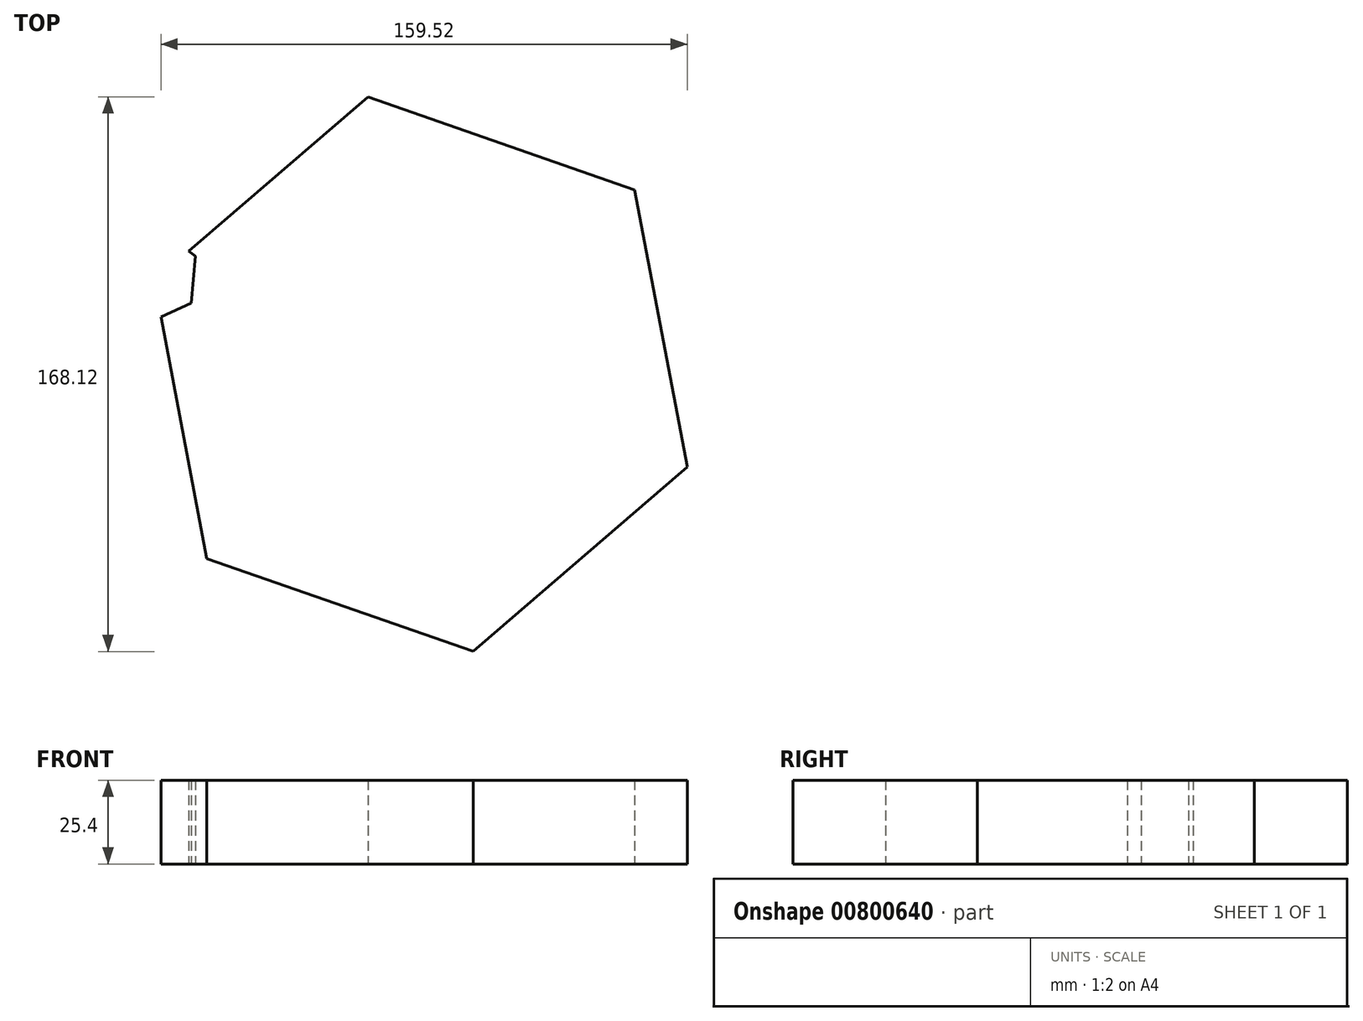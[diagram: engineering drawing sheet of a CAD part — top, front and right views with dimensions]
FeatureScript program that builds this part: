
annotation { "Feature Type Name" : "Feature", "Feature Type Description" : "" }
export const myFeature = defineFeature(function(context is Context, id is Id, definition is map)
    precondition{}
    {
        {
            var Q0;
            Q0=qCreatedBy(makeId("Top.planeOp"),FACE);
            var sketch = newSketch(context, id + "F0", { "sketchPlane" : qUnion([Q0])});
            skCircle(sketch, "E0.cCircle", {"center": v(0, 0) * mm, "radius": 74.1 * mm, "construction": true});
            skLineSegment(sketch, "E0.0", {"start": v(-16, 84.06) * mm, "end": v(64.8, 55.88) * mm});
            skLineSegment(sketch, "E0.1", {"start": v(64.8, 55.88) * mm, "end": v(80.8, -28.17) * mm});
            skLineSegment(sketch, "E0.2", {"start": v(80.8, -28.17) * mm, "end": v(16, -84.06) * mm});
            skLineSegment(sketch, "E0.3", {"start": v(16, -84.06) * mm, "end": v(-64.8, -55.88) * mm});
            skLineSegment(sketch, "E0.4", {"start": v(-64.8, -55.88) * mm, "end": v(-80.8, 28.17) * mm});
            skLineSegment(sketch, "E0.5", {"start": v(-80.8, 28.17) * mm, "end": v(-16, 84.06) * mm});
            skPoint(sketch, "E0.0.midPoint", {"position": v(24.4, 69.97) * mm});
            skCircle(sketch, "E1.cCircle", {"center": v(-81.17, 29.82) * mm, "radius": 12.37 * mm, "construction": true});
            skLineSegment(sketch, "E1.0", {"start": v(-68.2, 35.82) * mm, "end": v(-69.5, 21.59) * mm});
            skLineSegment(sketch, "E1.1", {"start": v(-69.5, 21.59) * mm, "end": v(-82.46, 15.59) * mm});
            skLineSegment(sketch, "E1.2", {"start": v(-82.46, 15.59) * mm, "end": v(-94.14, 23.82) * mm});
            skLineSegment(sketch, "E1.3", {"start": v(-94.14, 23.82) * mm, "end": v(-92.85, 38.05) * mm});
            skLineSegment(sketch, "E1.4", {"start": v(-92.85, 38.05) * mm, "end": v(-79.88, 44.05) * mm});
            skLineSegment(sketch, "E1.5", {"start": v(-79.88, 44.05) * mm, "end": v(-68.2, 35.82) * mm});
            skPoint(sketch, "E1.0.midPoint", {"position": v(-68.85, 28.7) * mm});
            skSolve(sketch);
        }
        {
            var Q0;
            {var subQ1=sQuery(id+"F0.wireOp",EDGE,"E0.0");Q0=makeQuery(id+"F0.imprint","IMPRINT",FACE,{"disambiguationData":[TD([[makeQuery(id+"F0.imprint","IMPRINT",EDGE,{"derivedFrom":subQ1}),-1.0]])]});}
            extrude(context, id + "F1", {"entities" : qUnion([Q0]), "depth" : 25.4 * mm, "offsetDistance" : 25.4 * mm});
        }
    });
